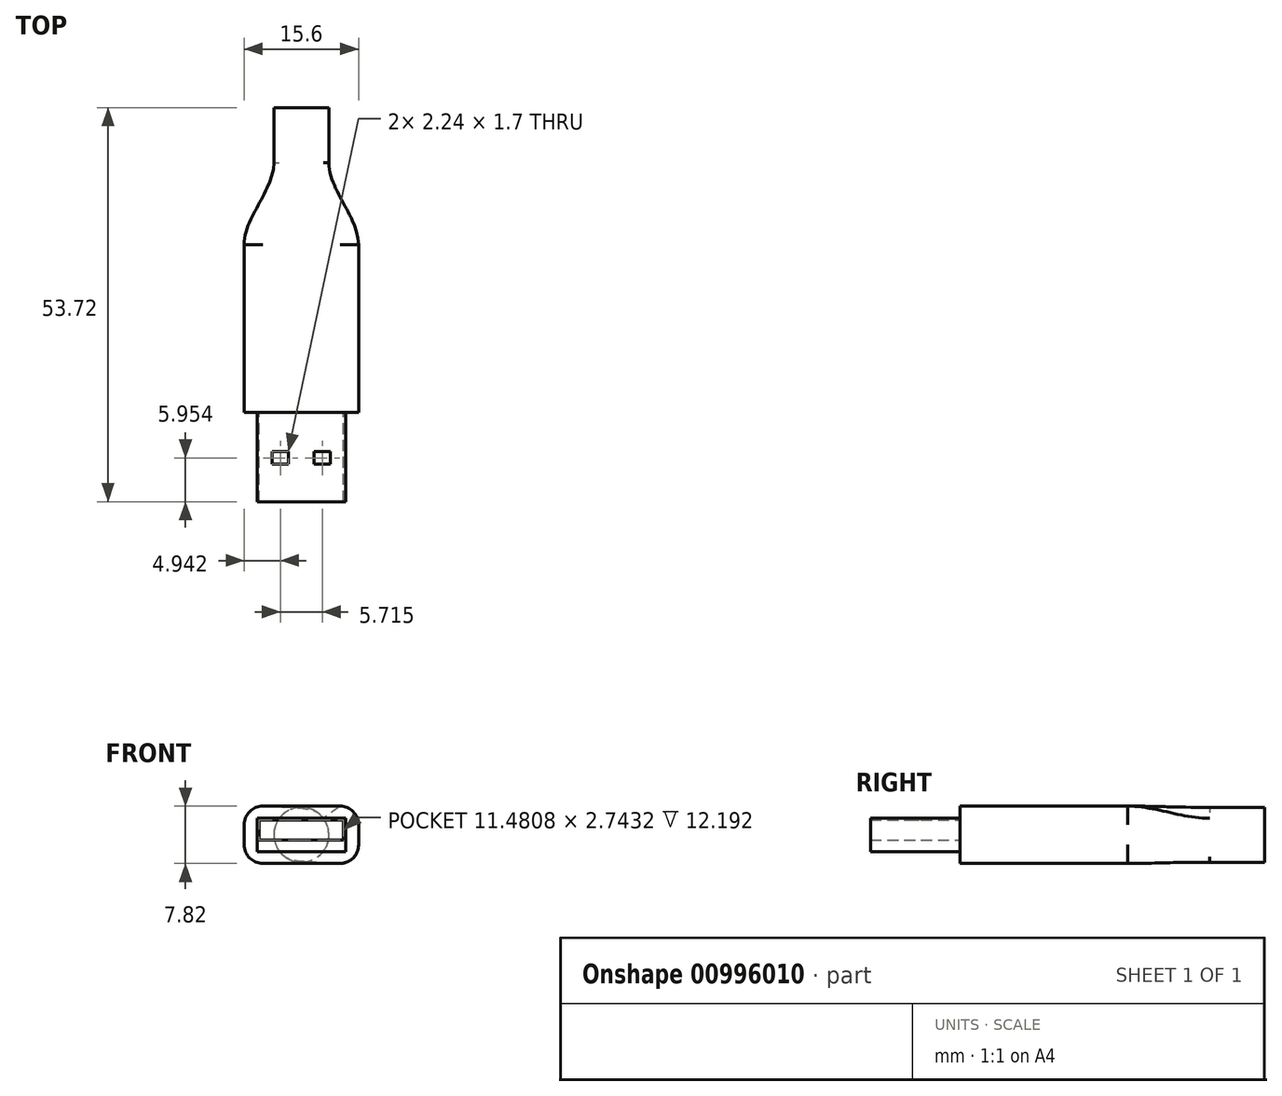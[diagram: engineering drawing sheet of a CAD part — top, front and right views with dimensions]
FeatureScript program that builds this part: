
annotation { "Feature Type Name" : "Feature", "Feature Type Description" : "" }
export const myFeature = defineFeature(function(context is Context, id is Id, definition is map)
    precondition{}
    {
        {
            var Q0;
            Q0=qCreatedBy(makeId("Front.planeOp"),FACE);
            var sketch = newSketch(context, id + "F0", { "sketchPlane" : qUnion([Q0])});
            skLineSegment(sketch, "E0.bottom", {"start": v(6.02, -2.29) * mm, "end": v(-6.02, -2.29) * mm});
            skLineSegment(sketch, "E0.top", {"start": v(6.02, 2.29) * mm, "end": v(-6.02, 2.29) * mm});
            skLineSegment(sketch, "E0.left", {"start": v(6.02, -2.29) * mm, "end": v(6.02, 2.29) * mm});
            skLineSegment(sketch, "E0.right", {"start": v(-6.02, -2.29) * mm, "end": v(-6.02, 2.29) * mm});
            skPoint(sketch, "E0.middle", {"position": v(0, 0) * mm});
            skSolve(sketch);
        }
        {
            var Q0;
            Q0=qSketchRegion(id+"F0",true);
            extrude(context, id + "F1", {"entities" : qUnion([Q0]), "depth" : 12.2 * mm, "offsetDistance" : 25.4 * mm});
        }
        {
            var Q0;
            Q0=makeQuery(id+"F1.opExtrude","CAP_FACE",FACE,{"disambiguationData":[OSD([sQuery(id+"F0.wireOp",EDGE,"E0.bottom"),sQuery(id+"F0.wireOp",EDGE,"E0.top"),sQuery(id+"F0.wireOp",EDGE,"E0.left"),sQuery(id+"F0.wireOp",EDGE,"E0.right")])],"isStart":false});
            var Q1;
            Q1=makeQuery(id+"F1.opExtrude","CAP_FACE",FACE,{"disambiguationData":[OSD([sQuery(id+"F0.wireOp",EDGE,"E0.bottom"),sQuery(id+"F0.wireOp",EDGE,"E0.top"),sQuery(id+"F0.wireOp",EDGE,"E0.left"),sQuery(id+"F0.wireOp",EDGE,"E0.right")])],"isStart":true});
            shell(context, id + "F2", {"entities" : qUnion([Q0, Q1]), "thickness" : 0.28 * mm});
        }
        {
            var Q0;
            Q0=qCreatedBy(makeId("Front.planeOp"),FACE);
            var sketch = newSketch(context, id + "F3", { "sketchPlane" : qUnion([Q0])});
            skLineSegment(sketch, "E1.bottom", {"start": v(5.26, 3.91) * mm, "end": v(-5.26, 3.91) * mm});
            skLineSegment(sketch, "E1.top", {"start": v(5.26, -3.91) * mm, "end": v(-5.26, -3.91) * mm});
            skLineSegment(sketch, "E1.left", {"start": v(7.8, 1.37) * mm, "end": v(7.8, -1.37) * mm});
            skLineSegment(sketch, "E1.right", {"start": v(-7.8, 1.37) * mm, "end": v(-7.8, -1.37) * mm});
            skPoint(sketch, "E1.middle", {"position": v(0, 0) * mm});
            skPoint(sketch, "E2.visualSharp", {"position": v(-7.8, 3.91) * mm});
            skArc(sketch, "E2.filletArc", {"start": v(-5.26, 3.91) * mm, "mid": v(-7.05, 3.17) * mm, "end": v(-7.8, 1.37) * mm});
            skPoint(sketch, "E3.visualSharp", {"position": v(7.8, 3.91) * mm});
            skArc(sketch, "E3.filletArc", {"start": v(7.8, 1.37) * mm, "mid": v(7.05, 3.17) * mm, "end": v(5.26, 3.91) * mm});
            skPoint(sketch, "E4.visualSharp", {"position": v(7.8, -3.91) * mm});
            skArc(sketch, "E4.filletArc", {"start": v(5.26, -3.91) * mm, "mid": v(7.05, -3.17) * mm, "end": v(7.8, -1.37) * mm});
            skPoint(sketch, "E5.visualSharp", {"position": v(-7.8, -3.91) * mm});
            skArc(sketch, "E5.filletArc", {"start": v(-7.8, -1.37) * mm, "mid": v(-7.05, -3.17) * mm, "end": v(-5.26, -3.91) * mm});
            skSolve(sketch);
        }
        {
            var Q0;
            Q0=qSketchRegion(id+"F3",true);
            extrude(context, id + "F4", {"entities" : qUnion([Q0]), "operationType" : NewBodyOperationType.ADD, "oppositeDirection" : true, "depth" : 22.86 * mm, "offsetDistance" : 25.4 * mm});
        }
        {
            var Q0;
            Q0=makeQuery(id+"F2.opShell","OFFSET_FACE",FACE,{"disambiguationData":[OSD([sQuery(id+"F0.wireOp",EDGE,"E0.bottom")])]});
            var sketch = newSketch(context, id + "F5", { "sketchPlane" : qUnion([Q0])});
            skLineSegment(sketch, "E6.0", {"start": v(-5.74, -12.2) * mm, "end": v(-5.74, 0) * mm});
            skLineSegment(sketch, "E6.1", {"start": v(5.74, 0) * mm, "end": v(-5.74, 0) * mm});
            skLineSegment(sketch, "E6.2", {"start": v(5.74, -12.2) * mm, "end": v(5.74, 0) * mm});
            skLineSegment(sketch, "E6.3", {"start": v(5.74, -12.2) * mm, "end": v(-5.74, -12.2) * mm});
            skSolve(sketch);
        }
        {
            var Q0;
            Q0=makeQuery(id+"F5.imprint","IMPRINT",FACE,{"disambiguationData":[TD([[makeQuery(id+"F5.imprint","IMPRINT",EDGE,{"derivedFrom":sQuery(id+"F5.wireOp",EDGE,"E6.0")}),-1.0]])]});
            extrude(context, id + "F6", {"entities" : qUnion([Q0]), "operationType" : NewBodyOperationType.ADD, "depth" : 1.27 * mm, "offsetDistance" : 25.4 * mm});
        }
        {
            var Q0;
            Q0=makeQuery(id+"F1.opExtrude","SWEPT_FACE",FACE,{"disambiguationData":[OSD([sQuery(id+"F0.wireOp",EDGE,"E0.top")])]});
            var sketch = newSketch(context, id + "F7", { "sketchPlane" : qUnion([Q0])});
            skLineSegment(sketch, "E7.bottom", {"start": v(-1.74, -7.09) * mm, "end": v(-3.98, -7.09) * mm});
            skLineSegment(sketch, "E7.top", {"start": v(-1.74, -5.38) * mm, "end": v(-3.98, -5.38) * mm});
            skLineSegment(sketch, "E7.left", {"start": v(-1.74, -7.09) * mm, "end": v(-1.74, -5.38) * mm});
            skLineSegment(sketch, "E7.right", {"start": v(-3.98, -7.09) * mm, "end": v(-3.98, -5.38) * mm});
            skPoint(sketch, "E7.middle", {"position": v(-2.86, -6.24) * mm});
            skLineSegment(sketch, "E8.bottom", {"start": v(3.98, -7.09) * mm, "end": v(1.74, -7.09) * mm});
            skLineSegment(sketch, "E8.top", {"start": v(3.98, -5.38) * mm, "end": v(1.74, -5.38) * mm});
            skLineSegment(sketch, "E8.left", {"start": v(3.98, -7.09) * mm, "end": v(3.98, -5.38) * mm});
            skLineSegment(sketch, "E8.right", {"start": v(1.74, -7.09) * mm, "end": v(1.74, -5.38) * mm});
            skPoint(sketch, "E8.middle", {"position": v(2.86, -6.24) * mm});
            skLineSegment(sketch, "E9", {"start": v(0, 0) * mm, "end": v(0, -12.2) * mm, "construction": true});
            skSolve(sketch);
        }
        {
            var Q0;
            Q0=qSketchRegion(id+"F7",true);
            extrude(context, id + "F8", {"entities" : qUnion([Q0]), "operationType" : NewBodyOperationType.REMOVE, "endBound" : BoundingType.UP_TO_NEXT, "oppositeDirection" : true, "depth" : 25.4 * mm, "offsetDistance" : 25.4 * mm});
        }
        {
            var Q0;
            {var subQ0=sQuery(id+"F3.wireOp",EDGE,"E3.filletArc");var subQ1=sQuery(id+"F3.wireOp",EDGE,"E1.right");var subQ2=sQuery(id+"F3.wireOp",EDGE,"E1.left");var subQ3=sQuery(id+"F3.wireOp",EDGE,"E1.top");var subQ4=sQuery(id+"F3.wireOp",EDGE,"E2.filletArc");var subQ5=sQuery(id+"F3.wireOp",EDGE,"E1.bottom");var subQ6=sQuery(id+"F3.wireOp",EDGE,"E4.filletArc");var subQ7=sQuery(id+"F3.wireOp",EDGE,"E5.filletArc");Q0=makeQuery(id+"F4.boolean.opBoolean","SPLIT",FACE,{"disambiguationData":[TD([makeQuery(id+"F1.opExtrude","SWEPT_FACE",FACE,{"disambiguationData":[OSD([sQuery(id+"F0.wireOp",EDGE,"E0.bottom")])]})])],"derivedFrom":makeQuery(id+"F4.opExtrude","CAP_FACE",FACE,{"disambiguationData":[OSD([subQ5,subQ3,subQ2,subQ1,subQ4,subQ0,subQ6,subQ7])],"isStart":true})});}
            cPlane(context, id + "F9", {"entities" : qUnion([Q0]), "cplaneType" : CPlaneType.OFFSET, "offset" : 41.53 * mm, "oppositeDirection" : true, "width" : 152.4 * mm, "height" : 152.4 * mm});
        }
        {
            var Q0;
            Q0=qCreatedBy(id+"F9.planeOp",FACE);
            var sketch = newSketch(context, id + "F10", { "sketchPlane" : qUnion([Q0])});
            skCircle(sketch, "E10", {"center": v(0, 0) * mm, "radius": 3.75 * mm});
            skSolve(sketch);
        }
        {
            var Q0;
            Q0=makeQuery(id+"F10.imprint","IMPRINT",FACE,{"disambiguationData":[TD([[makeQuery(id+"F10.imprint","IMPRINT",EDGE,{"derivedFrom":sQuery(id+"F10.wireOp",EDGE,"E10")}),1.0]])]});
            extrude(context, id + "F11", {"entities" : qUnion([Q0]), "depth" : 7.5 * mm, "offsetDistance" : 25.4 * mm});
        }
        {
            var Q1;
            Q1=makeQuery(id+"F4.opExtrude","CAP_FACE",FACE,{"disambiguationData":[OSD([sQuery(id+"F3.wireOp",EDGE,"E1.bottom"),sQuery(id+"F3.wireOp",EDGE,"E1.top"),sQuery(id+"F3.wireOp",EDGE,"E1.left"),sQuery(id+"F3.wireOp",EDGE,"E1.right"),sQuery(id+"F3.wireOp",EDGE,"E2.filletArc"),sQuery(id+"F3.wireOp",EDGE,"E3.filletArc"),sQuery(id+"F3.wireOp",EDGE,"E4.filletArc"),sQuery(id+"F3.wireOp",EDGE,"E5.filletArc")])],"isStart":false});
            var Q2;
            Q2=makeQuery(id+"F11.opExtrude","CAP_FACE",FACE,{"disambiguationData":[OSD([sQuery(id+"F10.wireOp",EDGE,"E10")])],"isStart":false});
            loft(context, id + "F12", {"operationType" : NewBodyOperationType.ADD, "startCondition" : LoftEndDerivativeType.NORMAL_TO_PROFILE, "startMagnitude" : 1, "endCondition" : LoftEndDerivativeType.NORMAL_TO_PROFILE, "endMagnitude" : 1, "sheetProfilesArray" : [{ "sheetProfileEntities" : qUnion([Q1]) }, { "sheetProfileEntities" : qUnion([Q2]) }]});
        }
    });
